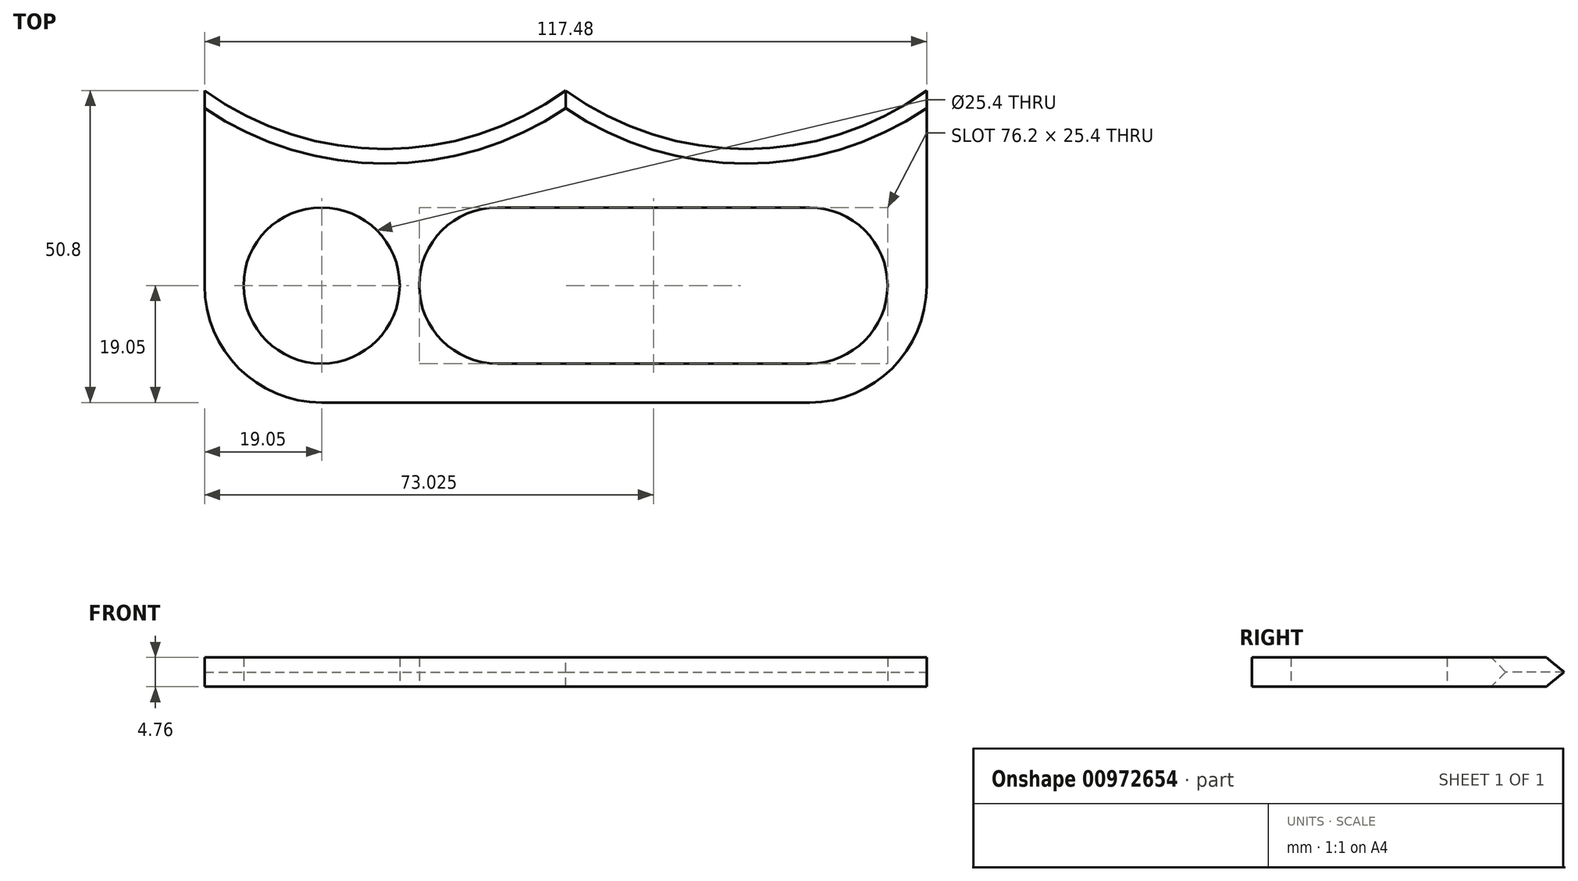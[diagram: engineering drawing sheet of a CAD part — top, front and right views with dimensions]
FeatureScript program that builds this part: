
annotation { "Feature Type Name" : "Feature", "Feature Type Description" : "" }
export const myFeature = defineFeature(function(context is Context, id is Id, definition is map)
    precondition{}
    {
        {
            var Q0;
            Q0=qCreatedBy(makeId("Top.planeOp"),FACE);
            var sketch = newSketch(context, id + "F0", { "sketchPlane" : qUnion([Q0])});
            skCircle(sketch, "E0", {"center": v(0, 0) * mm, "radius": 12.7 * mm});
            skArc(sketch, "E1", {"start": v(28.57, -12.7) * mm, "mid": v(15.88, 0) * mm, "end": v(28.58, 12.7) * mm});
            skLineSegment(sketch, "E2", {"start": v(28.58, 12.7) * mm, "end": v(79.38, 12.7) * mm});
            skLineSegment(sketch, "E3", {"start": v(28.58, -12.7) * mm, "end": v(79.38, -12.7) * mm});
            skArc(sketch, "E4", {"start": v(79.38, -12.7) * mm, "mid": v(92.08, 0) * mm, "end": v(79.38, 12.7) * mm});
            skArc(sketch, "E5", {"start": v(-19.05, 0) * mm, "mid": v(-13.47, -13.47) * mm, "end": v(0, -19.05) * mm});
            skArc(sketch, "E6", {"start": v(98.43, 0) * mm, "mid": v(92.85, -13.47) * mm, "end": v(79.38, -19.05) * mm});
            skLineSegment(sketch, "E7", {"start": v(0, -19.05) * mm, "end": v(79.38, -19.05) * mm});
            skLineSegment(sketch, "E8", {"start": v(0, -19.05) * mm, "end": v(0, 31.75) * mm, "construction": true});
            skLineSegment(sketch, "E9", {"start": v(-19.05, 0) * mm, "end": v(-19.05, 31.75) * mm});
            skLineSegment(sketch, "E10", {"start": v(98.43, 0) * mm, "end": v(98.43, 31.75) * mm});
            skLineSegment(sketch, "E11", {"start": v(-19.05, 31.75) * mm, "end": v(98.43, 31.75) * mm, "construction": true});
            skArc(sketch, "E12", {"start": v(-19.05, 31.75) * mm, "mid": v(10.32, 22.23) * mm, "end": v(39.69, 31.75) * mm});
            skArc(sketch, "E13", {"start": v(39.69, 31.75) * mm, "mid": v(69.06, 22.23) * mm, "end": v(98.43, 31.75) * mm});
            skPoint(sketch, "E14", {"position": v(69.06, 22.23) * mm});
            skPoint(sketch, "E15", {"position": v(10.32, 22.23) * mm});
            skSolve(sketch);
        }
        {
            var Q0;
            Q0=makeQuery(id+"F0.imprint","IMPRINT",FACE,{"disambiguationData":[TD([[makeQuery(id+"F0.imprint","IMPRINT",EDGE,{"derivedFrom":sQuery(id+"F0.wireOp",EDGE,"E0")}),-1.0]])]});
            extrude(context, id + "F1", {"entities" : qUnion([Q0]), "depth" : 4.76 * mm, "offsetDistance" : 25.4 * mm});
        }
        {
            var Q0;
            Q0=makeQuery(id+"F1.opExtrude","CAP_EDGE",EDGE,{"disambiguationData":[OSD([sQuery(id+"F0.wireOp",EDGE,"E12")])],"isStart":false});
            var Q1;
            Q1=makeQuery(id+"F1.opExtrude","CAP_EDGE",EDGE,{"disambiguationData":[OSD([sQuery(id+"F0.wireOp",EDGE,"E13")])],"isStart":false});
            var Q2;
            Q2=makeQuery(id+"F1.opExtrude","CAP_EDGE",EDGE,{"disambiguationData":[OSD([sQuery(id+"F0.wireOp",EDGE,"E13")])],"isStart":true});
            var Q3;
            Q3=makeQuery(id+"F1.opExtrude","CAP_EDGE",EDGE,{"disambiguationData":[OSD([sQuery(id+"F0.wireOp",EDGE,"E12")])],"isStart":true});
            chamfer(context, id + "F2", {"entities" : qUnion([Q0, Q1, Q2, Q3]), "width" : 2.38 * mm, "tangentPropagation" : true});
        }
    });
